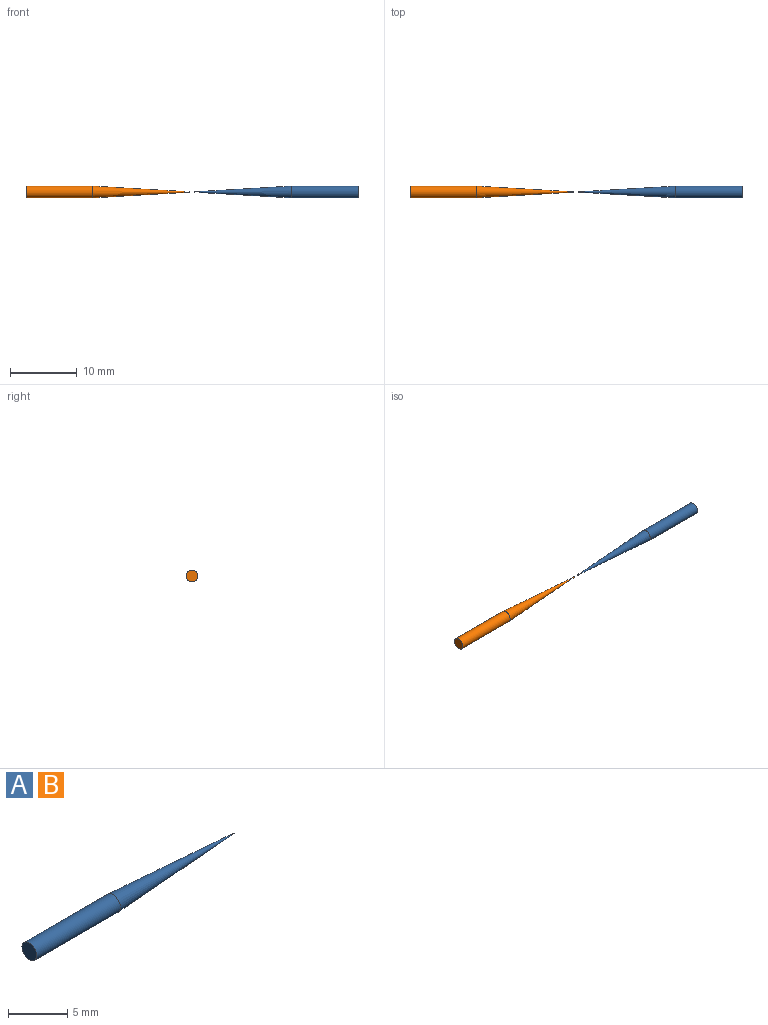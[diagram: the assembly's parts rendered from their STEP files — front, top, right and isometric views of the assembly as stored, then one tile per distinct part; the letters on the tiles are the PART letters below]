
ASSEMBLY  parts=2 mates=1
PART A: 4 faces, bbox 24.4x1.8x1.8 mm
  f0: plane 0.05x0.05mm, normal (1,0,0), area 0mm2, adj f1
  f1: cone r=0.03mm half-angle=3.4deg, axis (-1,0,0), area 40.8mm2, adj f0,f2
  f2: cylinder r=0.88mm len=10mm, axis (1,0,0), area 55mm2, adj f1,f3
  f3: plane 1.75x1.75mm, normal (-1,0,0), area 2.4mm2, adj f2
PART B: same geometry as A
PLACE A rot(axis=(0,1,0),180deg) t=(6.31,1.72,-10.18)mm
PLACE B t=(-23.32,1.72,-10.18)mm
MATE cylindrical A.f1 <-> B.f1  axis (-1,0,0) through (11.31,1.72,-10.18)mm
